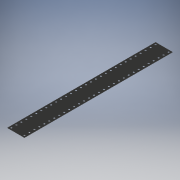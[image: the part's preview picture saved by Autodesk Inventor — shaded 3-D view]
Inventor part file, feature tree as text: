
AUTODESK INVENTOR PART (.ipt)
format: ipt  version: 2019 (Build 230136000, 136)  size: 183,296 bytes
history: native  units: mm
features: extrude x1, other x1
ambient origin geometry x8: Origin, YZ Plane, XZ Plane, XY Plane, X Axis, Y Axis, Z Axis, Center Point
bodies: Body1 (feature_tree)
feature tree (2):
  extrude  "Foam Body"  Depth=1639.0mm
  other  "Foam Scheme"
